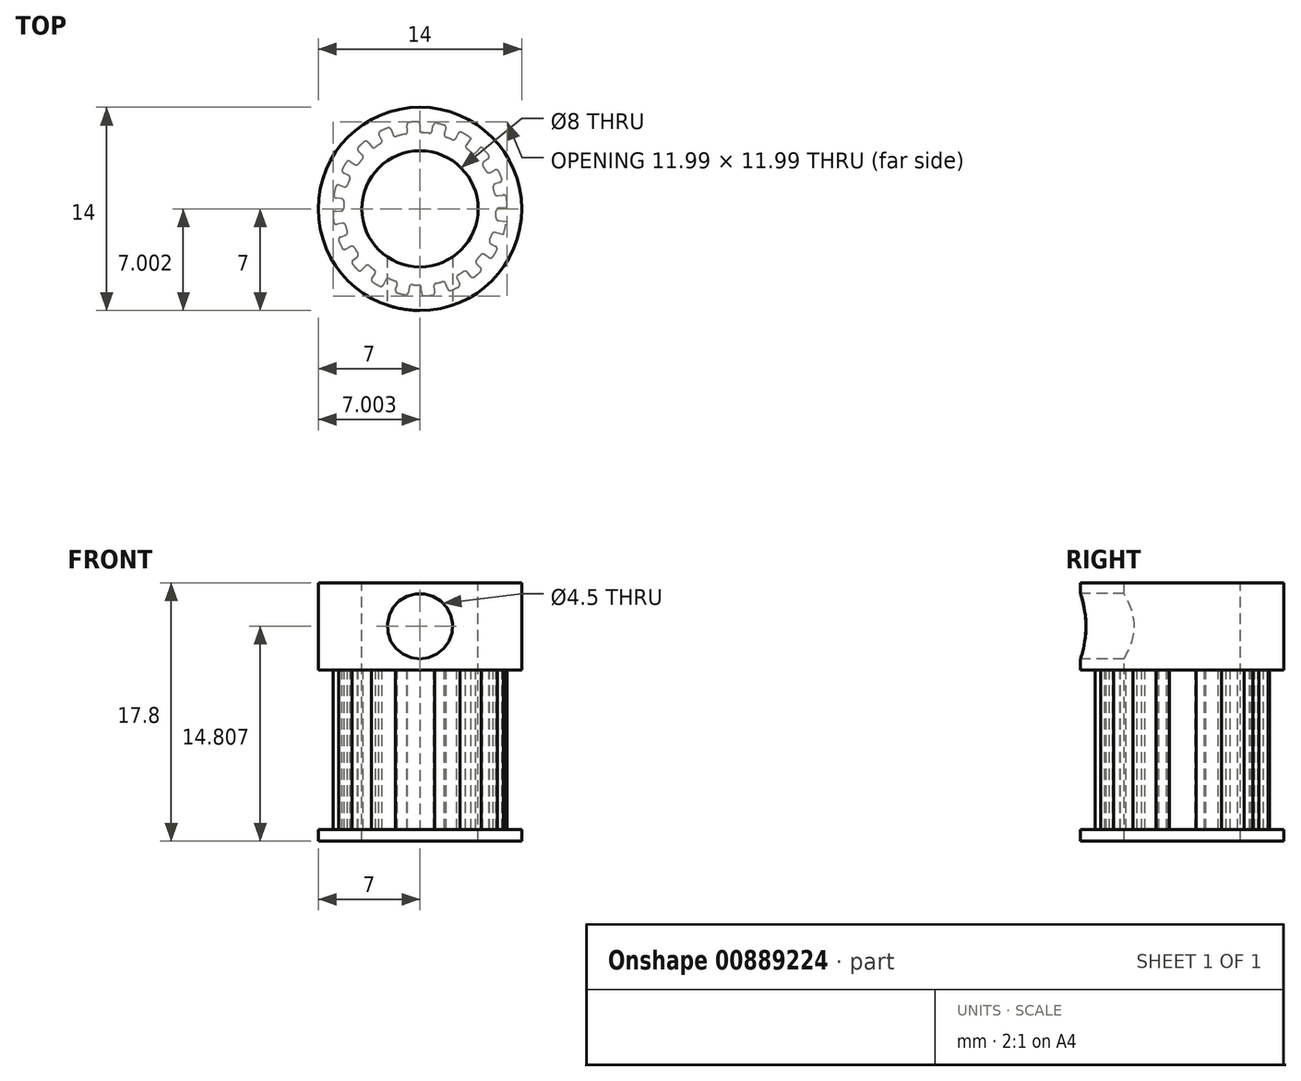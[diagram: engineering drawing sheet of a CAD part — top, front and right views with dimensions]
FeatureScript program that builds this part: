
annotation { "Feature Type Name" : "Feature", "Feature Type Description" : "" }
export const myFeature = defineFeature(function(context is Context, id is Id, definition is map)
    precondition{}
    {
        {
            var Q0;
            Q0=qCreatedBy(makeId("Front.planeOp"),FACE);
            cPlane(context, id + "F0", {"entities" : qUnion([Q0]), "cplaneType" : CPlaneType.OFFSET, "offset" : 7 * mm, "width" : 150 * mm, "height" : 150 * mm});
        }
        {
            var Q0;
            Q0=qCreatedBy(makeId("Top.planeOp"),FACE);
            cPlane(context, id + "F1", {"entities" : qUnion([Q0]), "cplaneType" : CPlaneType.OFFSET, "offset" : 11 * mm, "oppositeDirection" : true, "width" : 150 * mm, "height" : 150 * mm});
        }
        {
            var Q0;
            Q0=qCreatedBy(makeId("Top.planeOp"),FACE);
            var sketch = newSketch(context, id + "F2", { "sketchPlane" : qUnion([Q0])});
            skCircle(sketch, "E0", {"center": v(0, 0) * mm, "radius": 7 * mm});
            skSolve(sketch);
        }
        {
            var Q0;
            Q0=makeQuery(id+"F2.imprint","IMPRINT",FACE,{"disambiguationData":[TD([[makeQuery(id+"F2.imprint","IMPRINT",EDGE,{"derivedFrom":sQuery(id+"F2.wireOp",EDGE,"E0")}),1.0]])]});
            extrude(context, id + "F3", {"entities" : qUnion([Q0]), "depth" : 6 * mm, "offsetDistance" : 25 * mm});
        }
        {
            var Q0;
            Q0=qCreatedBy(makeId("Top.planeOp"),FACE);
            var sketch = newSketch(context, id + "F4", { "sketchPlane" : qUnion([Q0])});
            skCircle(sketch, "E1", {"center": v(0, 0) * mm, "radius": 4 * mm});
            skLineSegment(sketch, "E2", {"start": v(-0.82, 5.19) * mm, "end": v(-0.94, 5.93) * mm});
            skArc(sketch, "E3", {"start": v(0, 6) * mm, "mid": v(-0.47, 5.99) * mm, "end": v(-0.94, 5.93) * mm});
            skLineSegment(sketch, "E4", {"start": v(0, 6) * mm, "end": v(0, 5.25) * mm});
            skLineSegment(sketch, "E5.1.0", {"start": v(1.84, 5.7) * mm, "end": v(1.61, 5) * mm});
            skArc(sketch, "E5.1.1", {"start": v(1.84, 5.7) * mm, "mid": v(1.4, 5.84) * mm, "end": v(0.93, 5.93) * mm});
            skLineSegment(sketch, "E5.1.2", {"start": v(0.81, 5.19) * mm, "end": v(0.93, 5.93) * mm});
            skLineSegment(sketch, "E5.2.0", {"start": v(3.5, 4.87) * mm, "end": v(3.07, 4.26) * mm});
            skArc(sketch, "E5.2.1", {"start": v(3.5, 4.87) * mm, "mid": v(3.12, 5.13) * mm, "end": v(2.7, 5.36) * mm});
            skLineSegment(sketch, "E5.2.2", {"start": v(2.37, 4.69) * mm, "end": v(2.7, 5.36) * mm});
            skLineSegment(sketch, "E5.3.0", {"start": v(4.83, 3.55) * mm, "end": v(4.23, 3.1) * mm});
            skArc(sketch, "E5.3.1", {"start": v(4.83, 3.55) * mm, "mid": v(4.54, 3.92) * mm, "end": v(4.22, 4.27) * mm});
            skLineSegment(sketch, "E5.3.2", {"start": v(3.7, 3.73) * mm, "end": v(4.22, 4.27) * mm});
            skLineSegment(sketch, "E5.4.0", {"start": v(5.7, 1.9) * mm, "end": v(4.98, 1.66) * mm});
            skArc(sketch, "E5.4.1", {"start": v(5.7, 1.9) * mm, "mid": v(5.53, 2.34) * mm, "end": v(5.33, 2.76) * mm});
            skLineSegment(sketch, "E5.4.2", {"start": v(4.66, 2.42) * mm, "end": v(5.33, 2.76) * mm});
            skLineSegment(sketch, "E5.5.0", {"start": v(6, 0.06) * mm, "end": v(5.25, 0.05) * mm});
            skArc(sketch, "E5.5.1", {"start": v(6, 0.06) * mm, "mid": v(5.98, 0.53) * mm, "end": v(5.92, 1) * mm});
            skLineSegment(sketch, "E5.5.2", {"start": v(5.18, 0.87) * mm, "end": v(5.92, 1) * mm});
            skLineSegment(sketch, "E5.6.0", {"start": v(5.73, -1.8) * mm, "end": v(5.01, -1.57) * mm});
            skArc(sketch, "E5.6.1", {"start": v(5.73, -1.8) * mm, "mid": v(5.85, -1.34) * mm, "end": v(5.94, -0.87) * mm});
            skLineSegment(sketch, "E5.6.2", {"start": v(5.2, -0.76) * mm, "end": v(5.94, -0.87) * mm});
            skLineSegment(sketch, "E5.7.0", {"start": v(4.9, -3.46) * mm, "end": v(4.29, -3.03) * mm});
            skArc(sketch, "E5.7.1", {"start": v(4.9, -3.46) * mm, "mid": v(5.16, -3.07) * mm, "end": v(5.38, -2.65) * mm});
            skLineSegment(sketch, "E5.7.2", {"start": v(4.7, -2.32) * mm, "end": v(5.38, -2.65) * mm});
            skLineSegment(sketch, "E5.8.0", {"start": v(3.6, -4.8) * mm, "end": v(3.15, -4.2) * mm});
            skArc(sketch, "E5.8.1", {"start": v(3.6, -4.8) * mm, "mid": v(3.97, -4.5) * mm, "end": v(4.3, -4.18) * mm});
            skLineSegment(sketch, "E5.8.2", {"start": v(3.77, -3.66) * mm, "end": v(4.3, -4.18) * mm});
            skLineSegment(sketch, "E5.9.0", {"start": v(1.95, -5.67) * mm, "end": v(1.7, -4.97) * mm});
            skArc(sketch, "E5.9.1", {"start": v(1.95, -5.67) * mm, "mid": v(2.39, -5.5) * mm, "end": v(2.81, -5.3) * mm});
            skLineSegment(sketch, "E5.9.2", {"start": v(2.46, -4.64) * mm, "end": v(2.81, -5.3) * mm});
            skLineSegment(sketch, "E5.10.0", {"start": v(0.11, -6) * mm, "end": v(0.1, -5.25) * mm});
            skArc(sketch, "E5.10.1", {"start": v(0.11, -6) * mm, "mid": v(0.58, -5.98) * mm, "end": v(1.05, -5.9) * mm});
            skLineSegment(sketch, "E5.10.2", {"start": v(0.92, -5.17) * mm, "end": v(1.05, -5.9) * mm});
            skLineSegment(sketch, "E5.11.0", {"start": v(-1.74, -5.74) * mm, "end": v(-1.52, -5.02) * mm});
            skArc(sketch, "E5.11.1", {"start": v(-1.74, -5.74) * mm, "mid": v(-1.28, -5.86) * mm, "end": v(-0.82, -5.94) * mm});
            skLineSegment(sketch, "E5.11.2", {"start": v(-0.72, -5.2) * mm, "end": v(-0.82, -5.94) * mm});
            skLineSegment(sketch, "E5.12.0", {"start": v(-3.42, -4.93) * mm, "end": v(-3, -4.31) * mm});
            skArc(sketch, "E5.12.1", {"start": v(-3.42, -4.93) * mm, "mid": v(-3.02, -5.19) * mm, "end": v(-2.6, -5.4) * mm});
            skLineSegment(sketch, "E5.12.2", {"start": v(-2.28, -4.73) * mm, "end": v(-2.6, -5.4) * mm});
            skLineSegment(sketch, "E5.13.0", {"start": v(-4.77, -3.64) * mm, "end": v(-4.17, -3.19) * mm});
            skArc(sketch, "E5.13.1", {"start": v(-4.77, -3.64) * mm, "mid": v(-4.47, -4) * mm, "end": v(-4.14, -4.34) * mm});
            skLineSegment(sketch, "E5.13.2", {"start": v(-3.62, -3.8) * mm, "end": v(-4.14, -4.34) * mm});
            skLineSegment(sketch, "E5.14.0", {"start": v(-5.66, -2) * mm, "end": v(-4.95, -1.75) * mm});
            skArc(sketch, "E5.14.1", {"start": v(-5.66, -2) * mm, "mid": v(-5.49, -2.44) * mm, "end": v(-5.27, -2.86) * mm});
            skLineSegment(sketch, "E5.14.2", {"start": v(-4.61, -2.5) * mm, "end": v(-5.27, -2.86) * mm});
            skLineSegment(sketch, "E5.15.0", {"start": v(-6, -0.17) * mm, "end": v(-5.25, -0.14) * mm});
            skArc(sketch, "E5.15.1", {"start": v(-6, -0.17) * mm, "mid": v(-5.97, -0.64) * mm, "end": v(-5.9, -1.1) * mm});
            skLineSegment(sketch, "E5.15.2", {"start": v(-5.16, -0.96) * mm, "end": v(-5.9, -1.1) * mm});
            skLineSegment(sketch, "E5.16.0", {"start": v(-5.76, 1.69) * mm, "end": v(-5.04, 1.47) * mm});
            skArc(sketch, "E5.16.1", {"start": v(-5.76, 1.69) * mm, "mid": v(-5.88, 1.23) * mm, "end": v(-5.95, 0.76) * mm});
            skLineSegment(sketch, "E5.16.2", {"start": v(-5.2, 0.67) * mm, "end": v(-5.95, 0.76) * mm});
            skLineSegment(sketch, "E5.17.0", {"start": v(-4.96, 3.37) * mm, "end": v(-4.34, 2.95) * mm});
            skArc(sketch, "E5.17.1", {"start": v(-4.96, 3.37) * mm, "mid": v(-5.21, 2.98) * mm, "end": v(-5.43, 2.56) * mm});
            skLineSegment(sketch, "E5.17.2", {"start": v(-4.75, 2.24) * mm, "end": v(-5.43, 2.56) * mm});
            skLineSegment(sketch, "E5.18.0", {"start": v(-3.69, 4.73) * mm, "end": v(-3.22, 4.14) * mm});
            skArc(sketch, "E5.18.1", {"start": v(-3.69, 4.73) * mm, "mid": v(-4.05, 4.43) * mm, "end": v(-4.38, 4.1) * mm});
            skLineSegment(sketch, "E5.18.2", {"start": v(-3.83, 3.59) * mm, "end": v(-4.38, 4.1) * mm});
            skLineSegment(sketch, "E5.19.0", {"start": v(-2.05, 5.64) * mm, "end": v(-1.8, 4.93) * mm});
            skArc(sketch, "E5.19.1", {"start": v(-2.05, 5.64) * mm, "mid": v(-2.49, 5.46) * mm, "end": v(-2.9, 5.25) * mm});
            skLineSegment(sketch, "E5.19.2", {"start": v(-2.55, 4.6) * mm, "end": v(-2.9, 5.25) * mm});
            skLineSegment(sketch, "E5.anchor1", {"start": v(0, 0) * mm, "end": v(-0.08, 1) * mm, "construction": true});
            skLineSegment(sketch, "E5.anchor2", {"start": v(0, 0) * mm, "end": v(-0.42, 0.91) * mm, "construction": true});
            skArc(sketch, "E6", {"start": v(-2.28, -4.73) * mm, "mid": v(-1.9, -4.9) * mm, "end": v(-1.52, -5.02) * mm});
            skArc(sketch, "E7.trimOffspring", {"start": v(-0.72, -5.2) * mm, "mid": v(-0.31, -5.24) * mm, "end": v(0.1, -5.25) * mm});
            skArc(sketch, "E8.trimOffspring", {"start": v(0.92, -5.17) * mm, "mid": v(1.31, -5.08) * mm, "end": v(1.7, -4.97) * mm});
            skArc(sketch, "E9.trimOffspring", {"start": v(2.46, -4.64) * mm, "mid": v(2.81, -4.43) * mm, "end": v(3.15, -4.2) * mm});
            skArc(sketch, "E10.trimOffspring", {"start": v(3.77, -3.66) * mm, "mid": v(4.04, -3.35) * mm, "end": v(4.29, -3.03) * mm});
            skArc(sketch, "E11.trimOffspring", {"start": v(4.7, -2.32) * mm, "mid": v(4.87, -1.95) * mm, "end": v(5.01, -1.57) * mm});
            skArc(sketch, "E12.trimOffspring", {"start": v(5.2, -0.76) * mm, "mid": v(5.24, -0.36) * mm, "end": v(5.25, 0.05) * mm});
            skArc(sketch, "E13.trimOffspring", {"start": v(5.18, 0.87) * mm, "mid": v(5.1, 1.27) * mm, "end": v(4.98, 1.66) * mm});
            skArc(sketch, "E14.trimOffspring", {"start": v(4.66, 2.42) * mm, "mid": v(4.46, 2.77) * mm, "end": v(4.23, 3.1) * mm});
            skArc(sketch, "E15.trimOffspring", {"start": v(3.7, 3.73) * mm, "mid": v(3.4, 4) * mm, "end": v(3.07, 4.26) * mm});
            skArc(sketch, "E16.trimOffspring", {"start": v(2.37, 4.69) * mm, "mid": v(2, 4.86) * mm, "end": v(1.61, 5) * mm});
            skArc(sketch, "E17.trimOffspring", {"start": v(0.81, 5.19) * mm, "mid": v(0.4, 5.23) * mm, "end": v(0, 5.25) * mm});
            skArc(sketch, "E18.trimOffspring", {"start": v(-0.82, 5.19) * mm, "mid": v(-1.31, 5.08) * mm, "end": v(-1.8, 4.93) * mm});
            skArc(sketch, "E19.trimOffspring", {"start": v(-2.55, 4.6) * mm, "mid": v(-2.9, 4.38) * mm, "end": v(-3.22, 4.14) * mm});
            skArc(sketch, "E20.trimOffspring", {"start": v(-3.83, 3.59) * mm, "mid": v(-4.1, 3.28) * mm, "end": v(-4.34, 2.95) * mm});
            skArc(sketch, "E21.trimOffspring", {"start": v(-4.75, 2.24) * mm, "mid": v(-4.9, 1.86) * mm, "end": v(-5.04, 1.47) * mm});
            skArc(sketch, "E22.trimOffspring", {"start": v(-5.2, 0.67) * mm, "mid": v(-5.24, 0.26) * mm, "end": v(-5.25, -0.14) * mm});
            skArc(sketch, "E23.trimOffspring", {"start": v(-5.16, -0.96) * mm, "mid": v(-5.07, -1.36) * mm, "end": v(-4.95, -1.75) * mm});
            skArc(sketch, "E24.trimOffspring", {"start": v(-4.61, -2.5) * mm, "mid": v(-4.4, -2.85) * mm, "end": v(-4.17, -3.19) * mm});
            skArc(sketch, "E25.trimOffspring", {"start": v(-3.62, -3.8) * mm, "mid": v(-3.32, -4.07) * mm, "end": v(-3, -4.31) * mm});
            skSolve(sketch);
        }
        {
            var Q0;
            Q0=makeQuery(id+"F4.imprint","IMPRINT",FACE,{"disambiguationData":[TD([[makeQuery(id+"F4.imprint","IMPRINT",EDGE,{"derivedFrom":sQuery(id+"F4.wireOp",EDGE,"E1")}),-1.0]])]});
            extrude(context, id + "F5", {"entities" : qUnion([Q0]), "operationType" : NewBodyOperationType.ADD, "oppositeDirection" : true, "depth" : 11 * mm, "offsetDistance" : 25 * mm});
        }
        {
            var Q0;
            Q0=makeQuery(id+"F5.boolean.opBoolean","SPLIT",FACE,{"disambiguationData":[TD([makeQuery(id+"F5.opExtrude","SWEPT_FACE",FACE,{"disambiguationData":[OSD([sQuery(id+"F4.wireOp",EDGE,"E1")])]})])],"derivedFrom":makeQuery(id+"F3.opExtrude","CAP_FACE",FACE,{"disambiguationData":[OSD([sQuery(id+"F2.wireOp",EDGE,"E0")])],"isStart":true})});
            extrude(context, id + "F6", {"entities" : qUnion([Q0]), "operationType" : NewBodyOperationType.REMOVE, "oppositeDirection" : true, "depth" : 25 * mm, "offsetDistance" : 25 * mm});
        }
        {
            var Q0;
            Q0=makeQuery(id+"F5.opExtrude","SWEPT_EDGE",EDGE,{"disambiguationData":[OSD([sQuery(id+"F4.wireOp",EDGE,"E5.14.0"),sQuery(id+"F4.wireOp",EDGE,"E23.trimOffspring")])]});
            var Q1;
            Q1=makeQuery(id+"F5.opExtrude","SWEPT_EDGE",EDGE,{"disambiguationData":[OSD([sQuery(id+"F4.wireOp",EDGE,"E5.15.2"),sQuery(id+"F4.wireOp",EDGE,"E23.trimOffspring")])]});
            var Q2;
            Q2=makeQuery(id+"F5.opExtrude","SWEPT_EDGE",EDGE,{"disambiguationData":[OSD([sQuery(id+"F4.wireOp",EDGE,"E5.14.2"),sQuery(id+"F4.wireOp",EDGE,"E24.trimOffspring")])]});
            var Q3;
            Q3=makeQuery(id+"F5.opExtrude","SWEPT_EDGE",EDGE,{"disambiguationData":[OSD([sQuery(id+"F4.wireOp",EDGE,"E5.15.0"),sQuery(id+"F4.wireOp",EDGE,"E22.trimOffspring")])]});
            var Q4;
            Q4=makeQuery(id+"F5.opExtrude","SWEPT_EDGE",EDGE,{"disambiguationData":[OSD([sQuery(id+"F4.wireOp",EDGE,"E5.16.2"),sQuery(id+"F4.wireOp",EDGE,"E22.trimOffspring")])]});
            var Q5;
            Q5=makeQuery(id+"F5.opExtrude","SWEPT_EDGE",EDGE,{"disambiguationData":[OSD([sQuery(id+"F4.wireOp",EDGE,"E5.17.2"),sQuery(id+"F4.wireOp",EDGE,"E21.trimOffspring")])]});
            var Q6;
            Q6=makeQuery(id+"F5.opExtrude","SWEPT_EDGE",EDGE,{"disambiguationData":[OSD([sQuery(id+"F4.wireOp",EDGE,"E5.18.2"),sQuery(id+"F4.wireOp",EDGE,"E20.trimOffspring")])]});
            var Q7;
            Q7=makeQuery(id+"F5.opExtrude","SWEPT_EDGE",EDGE,{"disambiguationData":[OSD([sQuery(id+"F4.wireOp",EDGE,"E5.16.0"),sQuery(id+"F4.wireOp",EDGE,"E21.trimOffspring")])]});
            var Q8;
            Q8=makeQuery(id+"F5.opExtrude","SWEPT_EDGE",EDGE,{"disambiguationData":[OSD([sQuery(id+"F4.wireOp",EDGE,"E5.17.0"),sQuery(id+"F4.wireOp",EDGE,"E20.trimOffspring")])]});
            var Q9;
            Q9=makeQuery(id+"F5.opExtrude","SWEPT_EDGE",EDGE,{"disambiguationData":[OSD([sQuery(id+"F4.wireOp",EDGE,"E5.18.0"),sQuery(id+"F4.wireOp",EDGE,"E19.trimOffspring")])]});
            var Q10;
            Q10=makeQuery(id+"F5.opExtrude","SWEPT_EDGE",EDGE,{"disambiguationData":[OSD([sQuery(id+"F4.wireOp",EDGE,"E5.19.2"),sQuery(id+"F4.wireOp",EDGE,"E19.trimOffspring")])]});
            var Q11;
            Q11=makeQuery(id+"F5.opExtrude","SWEPT_EDGE",EDGE,{"disambiguationData":[OSD([sQuery(id+"F4.wireOp",EDGE,"E2"),sQuery(id+"F4.wireOp",EDGE,"E18.trimOffspring")])]});
            var Q12;
            Q12=makeQuery(id+"F5.opExtrude","SWEPT_EDGE",EDGE,{"disambiguationData":[OSD([sQuery(id+"F4.wireOp",EDGE,"E5.1.2"),sQuery(id+"F4.wireOp",EDGE,"E17.trimOffspring")])]});
            var Q13;
            Q13=makeQuery(id+"F5.opExtrude","SWEPT_EDGE",EDGE,{"disambiguationData":[OSD([sQuery(id+"F4.wireOp",EDGE,"E5.2.2"),sQuery(id+"F4.wireOp",EDGE,"E16.trimOffspring")])]});
            var Q14;
            Q14=makeQuery(id+"F5.opExtrude","SWEPT_EDGE",EDGE,{"disambiguationData":[OSD([sQuery(id+"F4.wireOp",EDGE,"E5.19.0"),sQuery(id+"F4.wireOp",EDGE,"E18.trimOffspring")])]});
            var Q15;
            Q15=makeQuery(id+"F5.opExtrude","SWEPT_EDGE",EDGE,{"disambiguationData":[OSD([sQuery(id+"F4.wireOp",EDGE,"E4"),sQuery(id+"F4.wireOp",EDGE,"E17.trimOffspring")])]});
            var Q16;
            Q16=makeQuery(id+"F5.opExtrude","SWEPT_EDGE",EDGE,{"disambiguationData":[OSD([sQuery(id+"F4.wireOp",EDGE,"E5.1.0"),sQuery(id+"F4.wireOp",EDGE,"E16.trimOffspring")])]});
            var Q17;
            Q17=makeQuery(id+"F5.opExtrude","SWEPT_EDGE",EDGE,{"disambiguationData":[OSD([sQuery(id+"F4.wireOp",EDGE,"E5.2.0"),sQuery(id+"F4.wireOp",EDGE,"E15.trimOffspring")])]});
            var Q18;
            Q18=makeQuery(id+"F5.opExtrude","SWEPT_EDGE",EDGE,{"disambiguationData":[OSD([sQuery(id+"F4.wireOp",EDGE,"E5.3.2"),sQuery(id+"F4.wireOp",EDGE,"E15.trimOffspring")])]});
            var Q19;
            Q19=makeQuery(id+"F5.opExtrude","SWEPT_EDGE",EDGE,{"disambiguationData":[OSD([sQuery(id+"F4.wireOp",EDGE,"E5.3.0"),sQuery(id+"F4.wireOp",EDGE,"E14.trimOffspring")])]});
            var Q20;
            Q20=makeQuery(id+"F5.opExtrude","SWEPT_EDGE",EDGE,{"disambiguationData":[OSD([sQuery(id+"F4.wireOp",EDGE,"E5.5.2"),sQuery(id+"F4.wireOp",EDGE,"E13.trimOffspring")])]});
            var Q21;
            Q21=makeQuery(id+"F5.opExtrude","SWEPT_EDGE",EDGE,{"disambiguationData":[OSD([sQuery(id+"F4.wireOp",EDGE,"E5.6.2"),sQuery(id+"F4.wireOp",EDGE,"E12.trimOffspring")])]});
            var Q22;
            Q22=makeQuery(id+"F5.opExtrude","SWEPT_EDGE",EDGE,{"disambiguationData":[OSD([sQuery(id+"F4.wireOp",EDGE,"E5.4.2"),sQuery(id+"F4.wireOp",EDGE,"E14.trimOffspring")])]});
            var Q23;
            Q23=makeQuery(id+"F5.opExtrude","SWEPT_EDGE",EDGE,{"disambiguationData":[OSD([sQuery(id+"F4.wireOp",EDGE,"E5.4.0"),sQuery(id+"F4.wireOp",EDGE,"E13.trimOffspring")])]});
            var Q24;
            Q24=makeQuery(id+"F5.opExtrude","SWEPT_EDGE",EDGE,{"disambiguationData":[OSD([sQuery(id+"F4.wireOp",EDGE,"E5.5.0"),sQuery(id+"F4.wireOp",EDGE,"E12.trimOffspring")])]});
            var Q25;
            Q25=makeQuery(id+"F5.opExtrude","SWEPT_EDGE",EDGE,{"disambiguationData":[OSD([sQuery(id+"F4.wireOp",EDGE,"E5.6.0"),sQuery(id+"F4.wireOp",EDGE,"E11.trimOffspring")])]});
            var Q26;
            Q26=makeQuery(id+"F5.opExtrude","SWEPT_EDGE",EDGE,{"disambiguationData":[OSD([sQuery(id+"F4.wireOp",EDGE,"E5.7.2"),sQuery(id+"F4.wireOp",EDGE,"E11.trimOffspring")])]});
            var Q27;
            Q27=makeQuery(id+"F5.opExtrude","SWEPT_EDGE",EDGE,{"disambiguationData":[OSD([sQuery(id+"F4.wireOp",EDGE,"E5.8.2"),sQuery(id+"F4.wireOp",EDGE,"E10.trimOffspring")])]});
            var Q28;
            Q28=makeQuery(id+"F5.opExtrude","SWEPT_EDGE",EDGE,{"disambiguationData":[OSD([sQuery(id+"F4.wireOp",EDGE,"E5.9.2"),sQuery(id+"F4.wireOp",EDGE,"E9.trimOffspring")])]});
            var Q29;
            Q29=makeQuery(id+"F5.opExtrude","SWEPT_EDGE",EDGE,{"disambiguationData":[OSD([sQuery(id+"F4.wireOp",EDGE,"E5.9.0"),sQuery(id+"F4.wireOp",EDGE,"E5.9.1")])]});
            var Q30;
            Q30=makeQuery(id+"F5.opExtrude","SWEPT_EDGE",EDGE,{"disambiguationData":[OSD([sQuery(id+"F4.wireOp",EDGE,"E5.7.0"),sQuery(id+"F4.wireOp",EDGE,"E10.trimOffspring")])]});
            var Q31;
            Q31=makeQuery(id+"F5.opExtrude","SWEPT_EDGE",EDGE,{"disambiguationData":[OSD([sQuery(id+"F4.wireOp",EDGE,"E5.8.0"),sQuery(id+"F4.wireOp",EDGE,"E9.trimOffspring")])]});
            var Q32;
            Q32=makeQuery(id+"F5.opExtrude","SWEPT_EDGE",EDGE,{"disambiguationData":[OSD([sQuery(id+"F4.wireOp",EDGE,"E5.9.0"),sQuery(id+"F4.wireOp",EDGE,"E8.trimOffspring")])]});
            var Q33;
            Q33=makeQuery(id+"F5.opExtrude","SWEPT_EDGE",EDGE,{"disambiguationData":[OSD([sQuery(id+"F4.wireOp",EDGE,"E5.10.0"),sQuery(id+"F4.wireOp",EDGE,"E7.trimOffspring")])]});
            var Q34;
            Q34=makeQuery(id+"F5.opExtrude","SWEPT_EDGE",EDGE,{"disambiguationData":[OSD([sQuery(id+"F4.wireOp",EDGE,"E5.12.2"),sQuery(id+"F4.wireOp",EDGE,"E6")])]});
            var Q35;
            Q35=makeQuery(id+"F5.opExtrude","SWEPT_EDGE",EDGE,{"disambiguationData":[OSD([sQuery(id+"F4.wireOp",EDGE,"E5.10.2"),sQuery(id+"F4.wireOp",EDGE,"E8.trimOffspring")])]});
            var Q36;
            Q36=makeQuery(id+"F5.opExtrude","SWEPT_EDGE",EDGE,{"disambiguationData":[OSD([sQuery(id+"F4.wireOp",EDGE,"E5.11.2"),sQuery(id+"F4.wireOp",EDGE,"E7.trimOffspring")])]});
            var Q37;
            Q37=makeQuery(id+"F5.opExtrude","SWEPT_EDGE",EDGE,{"disambiguationData":[OSD([sQuery(id+"F4.wireOp",EDGE,"E5.11.0"),sQuery(id+"F4.wireOp",EDGE,"E6")])]});
            var Q38;
            Q38=makeQuery(id+"F5.opExtrude","SWEPT_EDGE",EDGE,{"disambiguationData":[OSD([sQuery(id+"F4.wireOp",EDGE,"E5.12.0"),sQuery(id+"F4.wireOp",EDGE,"E25.trimOffspring")])]});
            var Q39;
            Q39=makeQuery(id+"F5.opExtrude","SWEPT_EDGE",EDGE,{"disambiguationData":[OSD([sQuery(id+"F4.wireOp",EDGE,"E5.13.2"),sQuery(id+"F4.wireOp",EDGE,"E25.trimOffspring")])]});
            var Q40;
            Q40=makeQuery(id+"F5.opExtrude","SWEPT_EDGE",EDGE,{"disambiguationData":[OSD([sQuery(id+"F4.wireOp",EDGE,"E5.13.0"),sQuery(id+"F4.wireOp",EDGE,"E24.trimOffspring")])]});
            fillet(context, id + "F7", {"entities" : qUnion([Q0, Q1, Q2, Q3, Q4, Q5, Q6, Q7, Q8, Q9, Q10, Q11, Q12, Q13, Q14, Q15, Q16, Q17, Q18, Q19, Q20, Q21, Q22, Q23, Q24, Q25, Q26, Q27, Q28, Q29, Q30, Q31, Q32, Q33, Q34, Q35, Q36, Q37, Q38, Q39, Q40]), "radius" : 0.2 * mm, "tangentPropagation" : true, "allowEdgeOverflow" : false});
        }
        {
            var Q0;
            Q0=makeQuery(id+"F5.opExtrude","SWEPT_EDGE",EDGE,{"disambiguationData":[OSD([sQuery(id+"F4.wireOp",EDGE,"E5.13.1"),sQuery(id+"F4.wireOp",EDGE,"E5.13.2")])]});
            var Q1;
            Q1=makeQuery(id+"F5.opExtrude","SWEPT_EDGE",EDGE,{"disambiguationData":[OSD([sQuery(id+"F4.wireOp",EDGE,"E5.13.0"),sQuery(id+"F4.wireOp",EDGE,"E5.13.1")])]});
            var Q2;
            Q2=makeQuery(id+"F5.opExtrude","SWEPT_EDGE",EDGE,{"disambiguationData":[OSD([sQuery(id+"F4.wireOp",EDGE,"E5.14.1"),sQuery(id+"F4.wireOp",EDGE,"E5.14.2")])]});
            var Q3;
            Q3=makeQuery(id+"F5.opExtrude","SWEPT_EDGE",EDGE,{"disambiguationData":[OSD([sQuery(id+"F4.wireOp",EDGE,"E5.14.0"),sQuery(id+"F4.wireOp",EDGE,"E5.14.1")])]});
            var Q4;
            Q4=makeQuery(id+"F5.opExtrude","SWEPT_EDGE",EDGE,{"disambiguationData":[OSD([sQuery(id+"F4.wireOp",EDGE,"E5.15.1"),sQuery(id+"F4.wireOp",EDGE,"E5.15.2")])]});
            var Q5;
            Q5=makeQuery(id+"F5.opExtrude","SWEPT_EDGE",EDGE,{"disambiguationData":[OSD([sQuery(id+"F4.wireOp",EDGE,"E5.15.0"),sQuery(id+"F4.wireOp",EDGE,"E5.15.1")])]});
            var Q6;
            Q6=makeQuery(id+"F5.opExtrude","SWEPT_EDGE",EDGE,{"disambiguationData":[OSD([sQuery(id+"F4.wireOp",EDGE,"E5.16.1"),sQuery(id+"F4.wireOp",EDGE,"E5.16.2")])]});
            var Q7;
            Q7=makeQuery(id+"F5.opExtrude","SWEPT_EDGE",EDGE,{"disambiguationData":[OSD([sQuery(id+"F4.wireOp",EDGE,"E5.10.1"),sQuery(id+"F4.wireOp",EDGE,"E5.10.2")])]});
            var Q8;
            Q8=makeQuery(id+"F5.opExtrude","SWEPT_EDGE",EDGE,{"disambiguationData":[OSD([sQuery(id+"F4.wireOp",EDGE,"E5.9.1"),sQuery(id+"F4.wireOp",EDGE,"E5.9.2")])]});
            var Q9;
            Q9=makeQuery(id+"F5.opExtrude","SWEPT_EDGE",EDGE,{"disambiguationData":[OSD([sQuery(id+"F4.wireOp",EDGE,"E5.8.0"),sQuery(id+"F4.wireOp",EDGE,"E5.8.1")])]});
            var Q10;
            Q10=makeQuery(id+"F5.opExtrude","SWEPT_EDGE",EDGE,{"disambiguationData":[OSD([sQuery(id+"F4.wireOp",EDGE,"E5.8.1"),sQuery(id+"F4.wireOp",EDGE,"E5.8.2")])]});
            var Q11;
            Q11=makeQuery(id+"F5.opExtrude","SWEPT_EDGE",EDGE,{"disambiguationData":[OSD([sQuery(id+"F4.wireOp",EDGE,"E5.7.0"),sQuery(id+"F4.wireOp",EDGE,"E5.7.1")])]});
            var Q12;
            Q12=makeQuery(id+"F5.opExtrude","SWEPT_EDGE",EDGE,{"disambiguationData":[OSD([sQuery(id+"F4.wireOp",EDGE,"E5.7.1"),sQuery(id+"F4.wireOp",EDGE,"E5.7.2")])]});
            var Q13;
            Q13=makeQuery(id+"F5.opExtrude","SWEPT_EDGE",EDGE,{"disambiguationData":[OSD([sQuery(id+"F4.wireOp",EDGE,"E5.5.0"),sQuery(id+"F4.wireOp",EDGE,"E5.5.1")])]});
            var Q14;
            Q14=makeQuery(id+"F5.opExtrude","SWEPT_EDGE",EDGE,{"disambiguationData":[OSD([sQuery(id+"F4.wireOp",EDGE,"E5.5.1"),sQuery(id+"F4.wireOp",EDGE,"E5.5.2")])]});
            var Q15;
            Q15=makeQuery(id+"F5.opExtrude","SWEPT_EDGE",EDGE,{"disambiguationData":[OSD([sQuery(id+"F4.wireOp",EDGE,"E5.4.0"),sQuery(id+"F4.wireOp",EDGE,"E5.4.1")])]});
            var Q16;
            Q16=makeQuery(id+"F5.opExtrude","SWEPT_EDGE",EDGE,{"disambiguationData":[OSD([sQuery(id+"F4.wireOp",EDGE,"E5.4.1"),sQuery(id+"F4.wireOp",EDGE,"E5.4.2")])]});
            var Q17;
            Q17=makeQuery(id+"F5.opExtrude","SWEPT_EDGE",EDGE,{"disambiguationData":[OSD([sQuery(id+"F4.wireOp",EDGE,"E5.3.0"),sQuery(id+"F4.wireOp",EDGE,"E5.3.1")])]});
            var Q18;
            Q18=makeQuery(id+"F5.opExtrude","SWEPT_EDGE",EDGE,{"disambiguationData":[OSD([sQuery(id+"F4.wireOp",EDGE,"E5.2.1"),sQuery(id+"F4.wireOp",EDGE,"E5.2.2")])]});
            var Q19;
            Q19=makeQuery(id+"F5.opExtrude","SWEPT_EDGE",EDGE,{"disambiguationData":[OSD([sQuery(id+"F4.wireOp",EDGE,"E5.1.0"),sQuery(id+"F4.wireOp",EDGE,"E5.1.1")])]});
            var Q20;
            Q20=makeQuery(id+"F5.opExtrude","SWEPT_EDGE",EDGE,{"disambiguationData":[OSD([sQuery(id+"F4.wireOp",EDGE,"E5.1.1"),sQuery(id+"F4.wireOp",EDGE,"E5.1.2")])]});
            var Q21;
            Q21=makeQuery(id+"F5.opExtrude","SWEPT_EDGE",EDGE,{"disambiguationData":[OSD([sQuery(id+"F4.wireOp",EDGE,"E3"),sQuery(id+"F4.wireOp",EDGE,"E4")])]});
            var Q22;
            Q22=makeQuery(id+"F5.opExtrude","SWEPT_EDGE",EDGE,{"disambiguationData":[OSD([sQuery(id+"F4.wireOp",EDGE,"E2"),sQuery(id+"F4.wireOp",EDGE,"E3")])]});
            var Q23;
            Q23=makeQuery(id+"F5.opExtrude","SWEPT_EDGE",EDGE,{"disambiguationData":[OSD([sQuery(id+"F4.wireOp",EDGE,"E5.19.0"),sQuery(id+"F4.wireOp",EDGE,"E5.19.1")])]});
            var Q24;
            Q24=makeQuery(id+"F5.opExtrude","SWEPT_EDGE",EDGE,{"disambiguationData":[OSD([sQuery(id+"F4.wireOp",EDGE,"E5.19.1"),sQuery(id+"F4.wireOp",EDGE,"E5.19.2")])]});
            var Q25;
            Q25=makeQuery(id+"F5.opExtrude","SWEPT_EDGE",EDGE,{"disambiguationData":[OSD([sQuery(id+"F4.wireOp",EDGE,"E5.18.0"),sQuery(id+"F4.wireOp",EDGE,"E5.18.1")])]});
            var Q26;
            Q26=makeQuery(id+"F5.opExtrude","SWEPT_EDGE",EDGE,{"disambiguationData":[OSD([sQuery(id+"F4.wireOp",EDGE,"E5.18.1"),sQuery(id+"F4.wireOp",EDGE,"E5.18.2")])]});
            var Q27;
            Q27=makeQuery(id+"F5.opExtrude","SWEPT_EDGE",EDGE,{"disambiguationData":[OSD([sQuery(id+"F4.wireOp",EDGE,"E5.17.0"),sQuery(id+"F4.wireOp",EDGE,"E5.17.1")])]});
            var Q28;
            Q28=makeQuery(id+"F5.opExtrude","SWEPT_EDGE",EDGE,{"disambiguationData":[OSD([sQuery(id+"F4.wireOp",EDGE,"E5.17.1"),sQuery(id+"F4.wireOp",EDGE,"E5.17.2")])]});
            var Q29;
            Q29=makeQuery(id+"F5.opExtrude","SWEPT_EDGE",EDGE,{"disambiguationData":[OSD([sQuery(id+"F4.wireOp",EDGE,"E5.16.0"),sQuery(id+"F4.wireOp",EDGE,"E5.16.1")])]});
            var Q30;
            Q30=makeQuery(id+"F5.opExtrude","SWEPT_EDGE",EDGE,{"disambiguationData":[OSD([sQuery(id+"F4.wireOp",EDGE,"E5.12.0"),sQuery(id+"F4.wireOp",EDGE,"E5.12.1")])]});
            var Q31;
            Q31=makeQuery(id+"F5.opExtrude","SWEPT_EDGE",EDGE,{"disambiguationData":[OSD([sQuery(id+"F4.wireOp",EDGE,"E5.12.1"),sQuery(id+"F4.wireOp",EDGE,"E5.12.2")])]});
            var Q32;
            Q32=makeQuery(id+"F5.opExtrude","SWEPT_EDGE",EDGE,{"disambiguationData":[OSD([sQuery(id+"F4.wireOp",EDGE,"E5.11.0"),sQuery(id+"F4.wireOp",EDGE,"E5.11.1")])]});
            var Q33;
            Q33=makeQuery(id+"F5.opExtrude","SWEPT_EDGE",EDGE,{"disambiguationData":[OSD([sQuery(id+"F4.wireOp",EDGE,"E5.11.1"),sQuery(id+"F4.wireOp",EDGE,"E5.11.2")])]});
            var Q34;
            Q34=makeQuery(id+"F5.opExtrude","SWEPT_EDGE",EDGE,{"disambiguationData":[OSD([sQuery(id+"F4.wireOp",EDGE,"E5.10.0"),sQuery(id+"F4.wireOp",EDGE,"E5.10.1")])]});
            fillet(context, id + "F8", {"entities" : qUnion([Q0, Q1, Q2, Q3, Q4, Q5, Q6, Q7, Q8, Q9, Q10, Q11, Q12, Q13, Q14, Q15, Q16, Q17, Q18, Q19, Q20, Q21, Q22, Q23, Q24, Q25, Q26, Q27, Q28, Q29, Q30, Q31, Q32, Q33, Q34]), "radius" : 0.2 * mm, "tangentPropagation" : true, "allowEdgeOverflow" : false});
        }
        {
            var Q0;
            Q0=qCreatedBy(id+"F1.planeOp",FACE);
            var sketch = newSketch(context, id + "F9", { "sketchPlane" : qUnion([Q0])});
            skCircle(sketch, "E26", {"center": v(0, 0) * mm, "radius": 7 * mm});
            skCircle(sketch, "E27", {"center": v(0, 0) * mm, "radius": 4 * mm});
            skSolve(sketch);
        }
        {
            var Q0;
            Q0=makeQuery(id+"F9.imprint","IMPRINT",FACE,{"disambiguationData":[TD([[makeQuery(id+"F9.imprint","IMPRINT",EDGE,{"derivedFrom":sQuery(id+"F9.wireOp",EDGE,"E26")}),1.0]])]});
            extrude(context, id + "F10", {"entities" : qUnion([Q0]), "operationType" : NewBodyOperationType.ADD, "oppositeDirection" : true, "depth" : 0.8 * mm, "offsetDistance" : 25 * mm});
        }
        {
            var Q0;
            Q0=qCreatedBy(id+"F0.planeOp",FACE);
            var sketch = newSketch(context, id + "F11", { "sketchPlane" : qUnion([Q0])});
            skLineSegment(sketch, "E28", {"start": v(0, 6.01) * mm, "end": v(0, 0) * mm, "construction": true});
            skPoint(sketch, "E29", {"position": v(0, 3) * mm});
            skSolve(sketch);
        }
        {
            var Q0;
            Q0=sQuery(id+"F11.wireOp",VERTEX,"E29");
            var Q1;
            Q1=makeQuery(id+"F3.opExtrude","SWEPT_BODY",BODY,{"disambiguationData":[OSD([sQuery(id+"F2.wireOp",EDGE,"E0")])]});
            hole(context, id + "F12", {"style" : HoleStyle.SIMPLE, "endStyle" : HoleEndStyle.BLIND, "standardTappedOrClearance" : lookupTablePath({ "fit" : "Normal", "standard" : "ISO", "size" : "M4", "type" : "Clearance" }), "standardBlindInLast" : lookupTablePath({ "fit" : "Normal", "standard" : "ISO", "size" : "M4", "type" : "Clearance" }), "holeDiameter" : 4.5 * mm, "majorDiameter" : 5 * mm, "holeDepth" : 4 * mm, "tappedDepth" : 12 * mm, "tapClearance" : 3, "locations" : qUnion([Q0]), "scope" : qUnion([Q1])});
        }
    });
